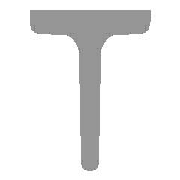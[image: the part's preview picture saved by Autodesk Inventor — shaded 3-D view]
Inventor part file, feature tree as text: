
AUTODESK INVENTOR PART (.ipt)
format: ipt  version: 2018 (Build 220112000, 112)  size: 154,624 bytes
history: native  units: mm (DEFAULTED — no unit token found)
features: other x4, sketch x3, plane x2
ambient origin geometry x7: Origin, YZ Plane, XY Plane, X Axis, Y Axis, Z Axis, Center Point
bodies: Solid1 (feature_tree), Body (feature_tree)
feature tree (9):
  parser-record x1  (decoder bookkeeping rows leaked as tree rows — omitted from the tree; the rows remain in map.json)
  other  "Driven Length"
  other  "Start plane"
  other  "End plane"
  plane  "WorkPlane3"
  sketch  "Sketch"  dims[d5=0.0mm d7=0.00349mm d8=2.75mm d9=3.85mm d10=2.75mm d11=3.85mm d12=0.00349mm d13=900.0mm d14=0.0mm d23=3.7mm d26=0.199973mm d27=0.199973mm d28=4.0mm d29=2.0mm d30=1.0mm d31=30.0mm d32=0.199973mm d33=30.0mm d34=8.5mm d35=-0.0mm d36=900.0mm d37=90.0deg d38=900.0mm]
  sketch  "Sketch3"  dims[d2=50.0mm]
  plane  "Work Plane6"
  sketch  "Sketch4"  dims[d4=0.00698mm]
